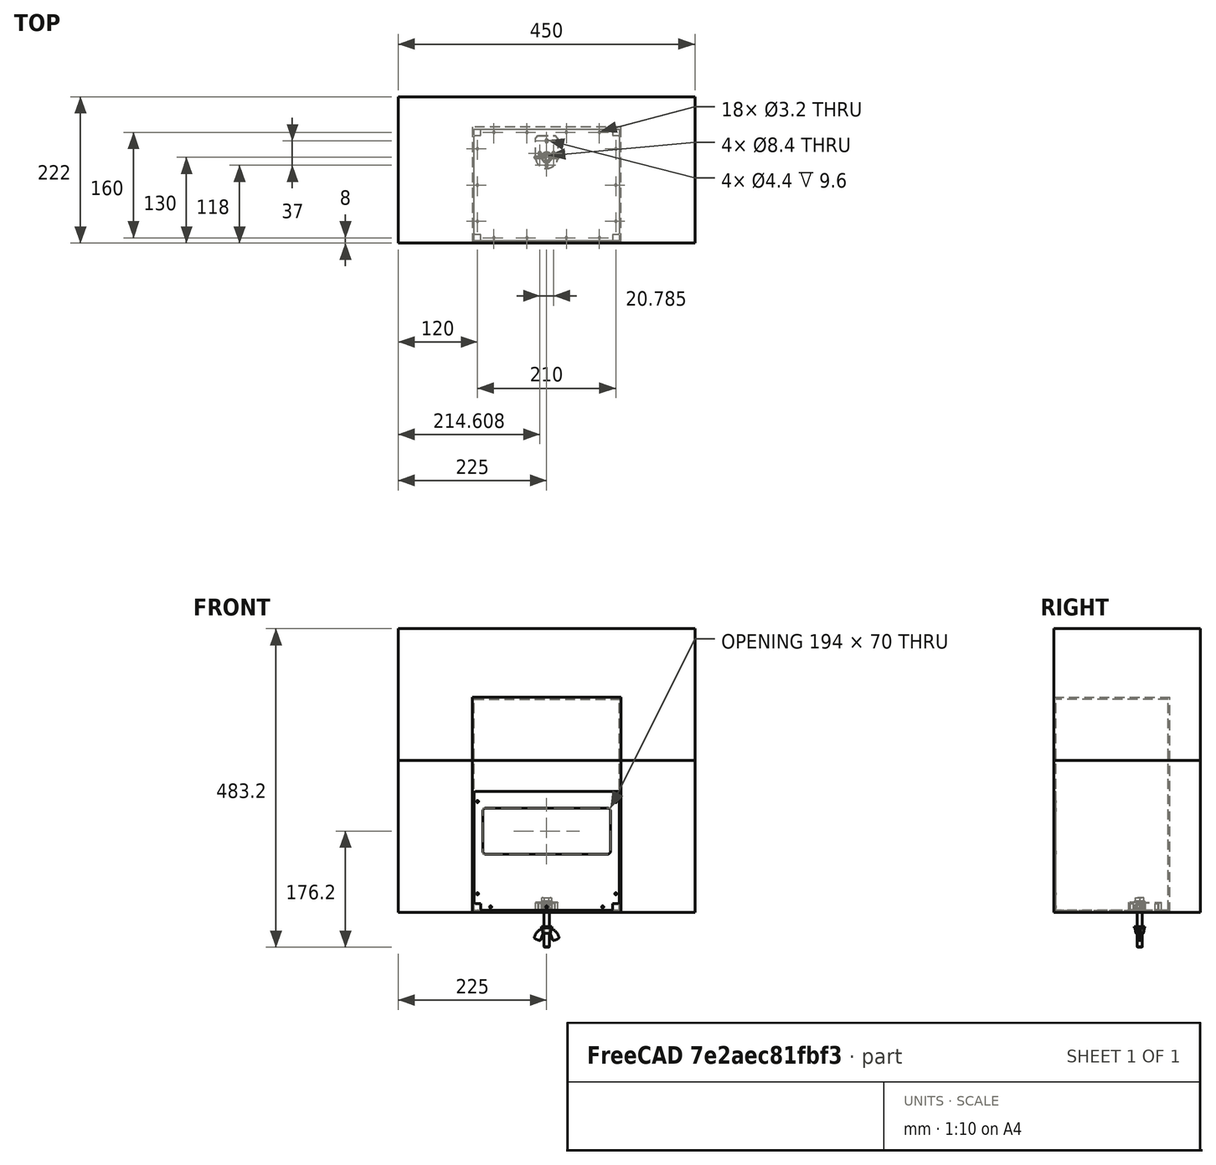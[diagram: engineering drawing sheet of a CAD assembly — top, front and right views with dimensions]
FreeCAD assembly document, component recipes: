
FREECAD ASSEMBLY — COMPONENT RECIPES ("basket_2023")

This assembly document has 8 components, labeled P0..P7 below (a component is one placed body or linked part). 6 of them carry a construction recipe — the FreeCAD feature program that regenerates the part from scratch, quoted from this document or its linked companion documents; the rest are supplied as boundary geometry only. No exploded tour is included for this assembly.
COMPONENT P0 — recipe-attached ("VolumeBasket", modeled in this document).
Construction recipe (the document's own serialized feature program — sketch geometry with constraints, then the solid features built on it; lengths are millimeters unless a unit is written):

FEATURE [Sketcher::SketchObject] Sketch
  ArcFitTolerance = 1e-06
  AttachmentSupport = -> [XY_Plane]
  ExternalBSplineMaxDegree = 5
  ExternalBSplineTolerance = 0.0001
  FullyConstrained = true
  InternalTolerance = 1e-06
  InvalidShape = false
  MakeInternals = true
  MapMode = 5
  Support = -> [XY_Plane]
  TreeRank = 12
  ValidateShape = true
  sketch-geometry (4):
    g0: LineSegment StartX=-113 StartY=3.262e-13 StartZ=0 EndX=113 EndY=1.84043e-10 EndZ=0
    g1: LineSegment StartX=113 StartY=1.84043e-10 StartZ=0 EndX=113 EndY=176 EndZ=0
    g2: LineSegment StartX=113 StartY=176 StartZ=0 EndX=-113 EndY=176 EndZ=0
    g3: LineSegment StartX=-113 StartY=176 StartZ=0 EndX=-113 EndY=3.126e-13 EndZ=0
  constraints (11):
    c: Coincident(g0,g1)
    c: Coincident(g1,g2)
    c: Coincident(g2,g3)
    c: Coincident(g3,g0)
    c: Horizontal(g2)
    c: Vertical(g1)
    c: Vertical(g3)
    c: PointOnObject(g0,g-1)
    c: Symmetric(g0,g0,g-2)
    c: DistanceX(g0,g0) = 226
    c: DistanceY(g1,g1) = 176
FEATURE [PartDesign::Pad] Pad
  AddSubType = 0
  AlongSketchNormal = false
  AutoTaperInnerAngle = true
  CheckUpToFaceLimits = true
  ClaimChildren = false
  Direction = (0,0,1)
  Fit = 0
  FitJoin = 0
  InnerFit = 0
  InnerFitJoin = 0
  InvalidShape = false
  Length = 326
  Length2 = 100
  Linearize = true
  NewSolid = false
  Profile = -> Sketch
  Refine = true
  Suppress = false
  TaperInnerAngle = 0
  TaperInnerAngleRev = 0
  TreeRank = 13
  Type = 0
  ValidateShape = true
  _ProfileBasedVersion = 1
FEATURE [PartDesign::Body] Body  label="VolumeBasket"
  AutoGroupSolids = false
  ClaimAllChildren = false
  ExportMode = 0
  Group = -> [Sketch,Pad]
  InvalidShape = false
  Origin = -> Origin
  SingleSolid = true
  Tip = -> Pad
  TreeRank = 11
  ValidateShape = true
  _ExportChildren = -> [Pad]
  _GroupVersion = 1
COMPONENT P1 — recipe-attached ("VolumeMakerBeam", modeled in this document).
Construction recipe (the document's own serialized feature program — sketch geometry with constraints, then the solid features built on it; lengths are millimeters unless a unit is written):

FEATURE [Sketcher::SketchObject] Sketch002
  ArcFitTolerance = 1e-06
  AttachmentOffset = pos=(0,0,3) rot=(0,0,1;0rad)
  AttachmentSupport = -> [XY_Plane002]
  ExternalBSplineMaxDegree = 5
  ExternalBSplineTolerance = 0.0001
  FullyConstrained = true
  InternalTolerance = 1e-06
  InvalidShape = false
  MakeInternals = true
  MapMode = 5
  Placement = pos=(0,0,3) rot=(0,0,1;0rad)
  Support = -> [XY_Plane002]
  TreeRank = 42
  ValidateShape = true
  sketch-geometry (4):
    g0: LineSegment StartX=-110 StartY=173 StartZ=0 EndX=110 EndY=173 EndZ=0
    g1: LineSegment StartX=110 StartY=173 StartZ=0 EndX=110 EndY=3 EndZ=0
    g2: LineSegment StartX=110 StartY=3 StartZ=0 EndX=-110 EndY=3 EndZ=0
    g3: LineSegment StartX=-110 StartY=3 StartZ=0 EndX=-110 EndY=173 EndZ=0
  constraints (11):
    c: Coincident(g0,g1)
    c: Coincident(g1,g2)
    c: Coincident(g2,g3)
    c: Coincident(g3,g0)
    c: Horizontal(g0)
    c: Vertical(g1)
    c: Vertical(g3)
    c: Symmetric(g1,g2,g-2)
    c: DistanceY(g-1,g1) = 3
    c: DistanceX(g2,g2) = 220
    c: DistanceY(g1,g1) = 170
FEATURE [PartDesign::Pad] Pad002
  AddSubType = 0
  AlongSketchNormal = false
  AutoTaperInnerAngle = true
  CheckUpToFaceLimits = true
  ClaimChildren = false
  Direction = (0,0,1)
  Fit = 0
  FitJoin = 0
  InnerFit = 0
  InnerFitJoin = 0
  InvalidShape = false
  Length = 320
  Length2 = 100
  Linearize = true
  NewSolid = false
  Profile = -> Sketch002
  Refine = true
  Suppress = false
  TaperInnerAngle = 0
  TaperInnerAngleRev = 0
  TreeRank = 43
  Type = 0
  ValidateShape = true
  _ProfileBasedVersion = 1
FEATURE [PartDesign::Body] Body002  label="VolumeMakerBeam"
  AutoGroupSolids = false
  ClaimAllChildren = false
  ExportMode = 0
  Group = -> [Sketch002,Pad002]
  InvalidShape = false
  Origin = -> Origin002
  SingleSolid = true
  Tip = -> Pad002
  TreeRank = 41
  ValidateShape = true
  _ExportChildren = -> [Pad002]
  _GroupVersion = 1
COMPONENT P2 — recipe-attached ("Volume300mm", modeled in this document).
Construction recipe (the document's own serialized feature program — sketch geometry with constraints, then the solid features built on it; lengths are millimeters unless a unit is written):

FEATURE [Sketcher::SketchObject] Sketch011
  ArcFitTolerance = 1e-06
  AttachmentSupport = -> [XZ_Plane006]
  ExternalBSplineMaxDegree = 5
  ExternalBSplineTolerance = 0.0001
  FullyConstrained = true
  InternalTolerance = 1e-06
  InvalidShape = false
  MakeInternals = true
  MapMode = 5
  Placement = pos=(0,0,0) rot=(1,0,0;1.5708rad)
  Support = -> [XZ_Plane006]
  TreeRank = 153
  ValidateShape = true
  sketch-geometry (4):
    g0: LineSegment StartX=-225 StartY=430 StartZ=0 EndX=225 EndY=430 EndZ=0
    g1: LineSegment StartX=225 StartY=430 StartZ=0 EndX=225 EndY=230 EndZ=0
    g2: LineSegment StartX=225 StartY=230 StartZ=0 EndX=-225 EndY=230 EndZ=0
    g3: LineSegment StartX=-225 StartY=230 StartZ=0 EndX=-225 EndY=430 EndZ=0
  constraints (11):
    c: Coincident(g0,g1)
    c: Coincident(g1,g2)
    c: Coincident(g2,g3)
    c: Coincident(g3,g0)
    c: Horizontal(g0)
    c: Vertical(g1)
    c: Vertical(g3)
    c: DistanceY(g0) = 430
    c: DistanceX(g0,g0) = 450
    c: Symmetric(g1,g2,g-2)
    c: DistanceY(g1) = 230
FEATURE [PartDesign::Pad] Pad007
  AddSubType = 0
  AlongSketchNormal = false
  AutoTaperInnerAngle = true
  CheckUpToFaceLimits = true
  ClaimChildren = false
  Direction = (0,-1,2e-16)
  Fit = 0
  FitJoin = 0
  InnerFit = 0
  InnerFitJoin = 0
  InvalidShape = false
  Length = 222
  Length2 = 100
  Linearize = true
  NewSolid = false
  Profile = -> Sketch011
  Refine = true
  Reversed = true
  Suppress = false
  TaperInnerAngle = 0
  TaperInnerAngleRev = 0
  TreeRank = 154
  Type = 0
  ValidateShape = true
  _ProfileBasedVersion = 1
FEATURE [PartDesign::Body] Body006  label="Volume300mm"
  AutoGroupSolids = false
  ClaimAllChildren = false
  ExportMode = 0
  Group = -> [Sketch011,Pad007]
  InvalidShape = false
  Origin = -> Origin009
  SingleSolid = true
  Tip = -> Pad007
  TreeRank = 152
  ValidateShape = true
  _ExportChildren = -> [Pad007]
  _GroupVersion = 1
COMPONENT P3 — recipe-attached ("Link(MB_300)", modeled in this document).
Construction recipe (the document's own serialized feature program — sketch geometry with constraints, then the solid features built on it; lengths are millimeters unless a unit is written):

FEATURE [Sketcher::SketchObject] Sketch006
  ArcFitTolerance = 1e-06
  AttachmentSupport = -> [XY_Plane004]
  ExternalBSplineMaxDegree = 5
  ExternalBSplineTolerance = 0.0001
  ExternalGeometry = -> [Pocket001]
  FullyConstrained = true
  InternalTolerance = 1e-06
  InvalidShape = false
  MakeInternals = true
  MapMode = 5
  Support = -> [XY_Plane004]
  TreeRank = 93
  ValidateShape = true
  sketch-geometry (5):
    g0: ArcOfCircle CenterX=-1.78743e-11 CenterY=130 CenterZ=0 NormalX=0 NormalY=0 NormalZ=1 AngleXU=0 Radius=17 StartAngle=3.14159 EndAngle=6.28319
    g1: LineSegment StartX=-17 StartY=130 StartZ=0 EndX=-17 EndY=163 EndZ=0
    g2: LineSegment StartX=-17 StartY=163 StartZ=0 EndX=17 EndY=163 EndZ=0
    g3: LineSegment StartX=17 StartY=163 StartZ=0 EndX=17 EndY=130 EndZ=0
    g4: Circle CenterX=-1.78743e-11 CenterY=130 CenterZ=0 NormalX=0 NormalY=0 NormalZ=1 AngleXU=0 Radius=4.2
  constraints (12):
    c: Coincident(g0,g-3)
    c: Vertical(g1)
    c: Coincident(g2,g1)
    c: Horizontal(g2)
    c: Coincident(g3,g2)
    c: Vertical(g3)
    c: DistanceY(g2,g-4) = 10
    c: Tangent(g3,g0) = 1.5708
    c: Tangent(g1,g0) = 1.5708
    c: Diameter(g0) = 34
    c: Coincident(g4,g0)
    c: Diameter(g4) = 8.4
FEATURE [PartDesign::Pad] Pad004
  AddSubType = 0
  AlongSketchNormal = false
  AutoTaperInnerAngle = true
  CheckUpToFaceLimits = true
  ClaimChildren = false
  Direction = (0,0,1)
  Fit = 0
  FitJoin = 0
  InnerFit = 0
  InnerFitJoin = 0
  InvalidShape = false
  Length = 12
  Length2 = 100
  Linearize = true
  NewSolid = false
  Profile = -> Sketch006
  Refine = true
  Suppress = false
  TaperInnerAngle = 0
  TaperInnerAngleRev = 0
  TreeRank = 104
  Type = 0
  ValidateShape = true
  _ProfileBasedVersion = 1
FEATURE [Sketcher::SketchObject] Sketch007
  ArcFitTolerance = 1e-06
  AttachmentSupport = -> [XY_Plane004]
  ExternalBSplineMaxDegree = 5
  ExternalBSplineTolerance = 0.0001
  ExternalGeometry = -> [Pad004]
  FullyConstrained = true
  InternalTolerance = 1e-06
  InvalidShape = false
  MakeInternals = true
  MapMode = 5
  Support = -> [XY_Plane004]
  TreeRank = 105
  ValidateShape = true
  sketch-geometry (7):
    g0: LineSegment StartX=7.79423 StartY=130 StartZ=0 EndX=3.89711 EndY=136.75 EndZ=0
    g1: LineSegment StartX=3.89711 StartY=136.75 StartZ=0 EndX=-3.89711 EndY=136.75 EndZ=0
    g2: LineSegment StartX=-3.89711 StartY=136.75 StartZ=0 EndX=-7.79423 EndY=130 EndZ=0
    g3: LineSegment StartX=-7.79423 StartY=130 StartZ=0 EndX=-3.89711 EndY=123.25 EndZ=0
    g4: LineSegment StartX=-3.89711 StartY=123.25 StartZ=0 EndX=3.89711 EndY=123.25 EndZ=0
    g5: LineSegment StartX=3.89711 StartY=123.25 StartZ=0 EndX=7.79423 EndY=130 EndZ=0
    g6: Circle [constr] CenterX=2.73045e-11 CenterY=130 CenterZ=0 NormalX=0 NormalY=0 NormalZ=1 AngleXU=0 Radius=7.79423
  constraints (16):
    c: Coincident(g0,g1)
    c: Coincident(g1,g2)
    c: Coincident(g2,g3)
    c: Coincident(g3,g4)
    c: Coincident(g4,g5)
    c: Coincident(g5,g0)
    c: Equal(g0, g1-g5) x5
    c: PointOnObject(g0,g6)
    c: PointOnObject(g1,g6)
    c: PointOnObject(g2,g6)
    c: PointOnObject(g3,g6)
    c: PointOnObject(g4,g6)
    c: PointOnObject(g5,g6)
    c: Coincident(g6,g-3)
    c: Horizontal(g1)
    c: DistanceY(g4,g0) = 13.5
FEATURE [PartDesign::Pad] Pad005
  AddSubType = 1
  AlongSketchNormal = false
  AutoTaperInnerAngle = true
  BaseFeature = -> Pad004
  CheckUpToFaceLimits = true
  ClaimChildren = false
  Direction = (0,0,1)
  Fit = 0
  FitJoin = 0
  InnerFit = 0
  InnerFitJoin = 0
  InvalidShape = false
  Length = 8.5
  Length2 = 100
  Linearize = true
  NewSolid = false
  Profile = -> Sketch007
  Refine = true
  Suppress = false
  TaperInnerAngle = 0
  TaperInnerAngleRev = 0
  TreeRank = 106
  Type = 0
  ValidateShape = true
  _ProfileBasedVersion = 1
FEATURE [Sketcher::SketchObject] Sketch008
  ArcFitTolerance = 1e-06
  AttachmentSupport = -> [XY_Plane004]
  ExternalBSplineMaxDegree = 5
  ExternalBSplineTolerance = 0.0001
  ExternalGeometry = -> [Pad004]
  FullyConstrained = true
  InternalTolerance = 1e-06
  InvalidShape = false
  MakeInternals = true
  MapMode = 5
  Support = -> [XY_Plane004]
  TreeRank = 107
  ValidateShape = true
  sketch-geometry (7):
    g0: Circle CenterX=1.1e-15 CenterY=118 CenterZ=0 NormalX=0 NormalY=0 NormalZ=1 AngleXU=0 Radius=2.2
    g1: Circle CenterX=-10.3923 CenterY=136 CenterZ=0 NormalX=0 NormalY=0 NormalZ=1 AngleXU=0 Radius=2.2
    g2: Circle CenterX=10.3923 CenterY=136 CenterZ=0 NormalX=0 NormalY=0 NormalZ=1 AngleXU=0 Radius=2.2
    g3: Circle [constr] CenterX=-4.19335e-11 CenterY=130 CenterZ=0 NormalX=0 NormalY=0 NormalZ=1 AngleXU=0 Radius=12
    g4: Circle CenterX=0 CenterY=155 CenterZ=0 NormalX=0 NormalY=0 NormalZ=1 AngleXU=0 Radius=2.2
    g5: LineSegment [constr] StartX=-1.80398e-11 StartY=130 StartZ=0 EndX=-10.3923 EndY=136 EndZ=0
    g6: LineSegment [constr] StartX=-1.79352e-11 StartY=130 StartZ=0 EndX=10.3923 EndY=136 EndZ=0
  constraints (18):
    c: PointOnObject(g0,g-2)
    c: Coincident(g3,g-3)
    c: PointOnObject(g2,g3)
    c: PointOnObject(g0,g3)
    c: PointOnObject(g1,g3)
    c: Equal(g1,g2)
    c: Equal(g1,g0)
    c: Diameter(g1) = 4.4
    c: PointOnObject(g4,g-2)
    c: Equal(g4,g2)
    c: Coincident(g5,g-3)
    c: Coincident(g5,g1)
    c: Coincident(g6,g-3)
    c: Coincident(g6,g2)
    c: Angle(g-2,g6) = 2.0944
    c: Angle(g5,g-2) = 2.0944
    c: DistanceY(g0,g-3) = 12
    c: DistanceY(g-3,g4) = 25
FEATURE [PartDesign::Pocket] Pocket002
  AddSubType = 1
  AutoTaperInnerAngle = true
  BaseFeature = -> Pad005
  CheckUpToFaceLimits = true
  ClaimChildren = false
  Fit = 0
  FitJoin = 0
  InnerFit = 0
  InnerFitJoin = 0
  InvalidShape = false
  Length = 10
  Length2 = 100
  Linearize = true
  NewSolid = false
  Profile = -> Sketch008
  Refine = true
  Reversed = true
  Suppress = false
  TaperInnerAngle = 0
  TaperInnerAngleRev = 0
  TreeRank = 108
  Type = 0
  ValidateShape = true
  _ProfileBasedVersion = 1
  _Version = 1
FEATURE [PartDesign::Chamfer] Chamfer001
  AddSubType = 0
  Angle = 45
  Base = -> Pocket002 [Edge8,Edge5]
  BaseFeature = -> Pocket002
  ChamferType = 0
  FlipDirection = false
  InvalidShape = false
  NewSolid = false
  Refine = true
  Size = 4
  Size2 = 1
  SupportTransform = false
  Suppress = false
  TreeRank = 119
  ValidateShape = true
FEATURE [PartDesign::Chamfer] Chamfer002
  AddSubType = 0
  Angle = 45
  Base = -> Chamfer001 [Face2,Edge50,Face5]
  BaseFeature = -> Chamfer001
  ChamferType = 0
  FlipDirection = false
  InvalidShape = false
  NewSolid = false
  Refine = true
  Size = 0.4
  Size2 = 1
  SupportTransform = false
  Suppress = false
  TreeRank = 120
  ValidateShape = true
FEATURE [PartDesign::Body] Body004  label="BlocVisPapillon"
  AutoGroupSolids = false
  ClaimAllChildren = false
  ExportMode = 0
  Group = -> [Sketch006,Pad004,Sketch007,Pad005,Sketch008,Pocket002,Chamfer001,Chamfer002]
  InvalidShape = false
  Origin = -> Origin005
  Placement = pos=(0,0,3) rot=(0,0,1;0rad)
  SingleSolid = true
  Tip = -> Chamfer002
  TreeRank = 136
  ValidateShape = true
  _ExportChildren = -> [Pad004,Pad005,Pocket002,Chamfer001,Chamfer002]
  _GroupVersion = 1
COMPONENT P4 — geometry summary ("Link001(MB_200)"; no construction recipe available for this part):
  bounding box: 200.0 x 10.0 x 10.0 mm
  tessellated surface: 288 triangles
  volume: 9738 mm^3 (49% of its bounding box)
  symmetry: 2-fold rotationally symmetric about the x axis; 4-fold rotationally symmetric about the y axis; 2-fold rotationally symmetric about the z axis; mirror-symmetric across its x mid-plane, y mid-plane, z mid-plane
COMPONENT P5 — geometry summary ("Link002(MB_150)"; no construction recipe available for this part):
  bounding box: 150.0 x 10.0 x 10.0 mm
  tessellated surface: 288 triangles
  volume: 7304 mm^3 (49% of its bounding box)
  symmetry: 2-fold rotationally symmetric about the x axis; 4-fold rotationally symmetric about the y axis; 2-fold rotationally symmetric about the z axis; mirror-symmetric across its y mid-plane, z mid-plane
COMPONENT P6 — recipe-attached ("Link003(Corner)", modeled in this document).
Construction recipe (the document's own serialized feature program — sketch geometry with constraints, then the solid features built on it; lengths are millimeters unless a unit is written):

FEATURE [Sketcher::SketchObject] Sketch001
  ArcFitTolerance = 1e-06
  AttachmentSupport = -> [XY_Plane001]
  ExternalBSplineMaxDegree = 5
  ExternalBSplineTolerance = 0.0001
  FullyConstrained = true
  InternalTolerance = 1e-06
  InvalidShape = false
  MakeInternals = true
  MapMode = 5
  Support = -> [XY_Plane001]
  TreeRank = 30
  ValidateShape = true
  sketch-geometry (4):
    g0: LineSegment StartX=-225 StartY=-3.837e-13 StartZ=0 EndX=225 EndY=-3.837e-13 EndZ=0
    g1: LineSegment StartX=225 StartY=-3.837e-13 StartZ=0 EndX=225 EndY=222 EndZ=0
    g2: LineSegment StartX=225 StartY=222 StartZ=0 EndX=-225 EndY=222 EndZ=0
    g3: LineSegment StartX=-225 StartY=222 StartZ=0 EndX=-225 EndY=-3.695e-13 EndZ=0
  constraints (11):
    c: Coincident(g0,g1)
    c: Coincident(g1,g2)
    c: Coincident(g2,g3)
    c: Coincident(g3,g0)
    c: Horizontal(g0)
    c: Horizontal(g2)
    c: Vertical(g1)
    c: Vertical(g3)
    c: Symmetric(g0,g0,g-1)
    c: DistanceY(g1,g1) = 222
    c: DistanceX(g0,g0) = 450
FEATURE [PartDesign::Pad] Pad001
  AddSubType = 0
  AlongSketchNormal = false
  AutoTaperInnerAngle = true
  CheckUpToFaceLimits = true
  ClaimChildren = false
  Direction = (0,0,1)
  Fit = 0
  FitJoin = 0
  InnerFit = 0
  InnerFitJoin = 0
  InvalidShape = false
  Length = 430
  Length2 = 100
  Linearize = true
  NewSolid = false
  Profile = -> Sketch001
  Refine = true
  Suppress = false
  TaperInnerAngle = 0
  TaperInnerAngleRev = 0
  TreeRank = 31
  Type = 0
  ValidateShape = true
  _ProfileBasedVersion = 1
FEATURE [PartDesign::Body] Body001  label="VolumeMax"
  AutoGroupSolids = false
  ClaimAllChildren = false
  ExportMode = 0
  Group = -> [Sketch001,Pad001]
  InvalidShape = false
  Origin = -> Origin001
  SingleSolid = true
  Tip = -> Pad001
  TreeRank = 29
  ValidateShape = true
  _ExportChildren = -> [Pad001]
  _GroupVersion = 1
COMPONENT P7 — recipe-attached ("Basket_2023", modeled in this document).
Construction recipe (the document's own serialized feature program — sketch geometry with constraints, then the solid features built on it; lengths are millimeters unless a unit is written):

FEATURE [Sketcher::SketchObject] Sketch010
  ArcFitTolerance = 1e-06
  AttachmentSupport = -> [XZ_Plane005]
  ExternalBSplineMaxDegree = 5
  ExternalBSplineTolerance = 0.0001
  FullyConstrained = true
  InternalTolerance = 1e-06
  InvalidShape = false
  MakeInternals = true
  MapMode = 5
  Placement = pos=(0,0,0) rot=(1,0,0;1.5708rad)
  Support = -> [XZ_Plane005]
  TreeRank = 131
  ValidateShape = true
  sketch-geometry (28):
    g0: LineSegment StartX=-100 StartY=3 StartZ=0 EndX=-100 EndY=13 EndZ=0
    g1: LineSegment StartX=-100 StartY=13 StartZ=0 EndX=-110 EndY=13 EndZ=0
    g2: LineSegment StartX=-110 StartY=13 StartZ=0 EndX=-110 EndY=183 EndZ=0
    g3: LineSegment StartX=-110 StartY=183 StartZ=0 EndX=110 EndY=183 EndZ=0
    g4: LineSegment StartX=110 StartY=183 StartZ=0 EndX=110 EndY=13 EndZ=0
    g5: LineSegment StartX=110 StartY=13 StartZ=0 EndX=100 EndY=13 EndZ=0
    g6: LineSegment StartX=100 StartY=13 StartZ=0 EndX=100 EndY=3 EndZ=0
    g7: LineSegment StartX=100 StartY=3 StartZ=0 EndX=-100 EndY=3 EndZ=0
    g8: ArcOfCircle CenterX=-92 CenterY=153 CenterZ=0 NormalX=0 NormalY=0 NormalZ=1 AngleXU=0 Radius=5 StartAngle=1.5708 EndAngle=3.14159
    g9: LineSegment StartX=-92 StartY=158 StartZ=0 EndX=92 EndY=158 EndZ=0
    g10: ArcOfCircle CenterX=92 CenterY=153 CenterZ=0 NormalX=0 NormalY=0 NormalZ=1 AngleXU=0 Radius=5 StartAngle=-9e-16 EndAngle=1.5708
    g11: LineSegment StartX=97 StartY=153 StartZ=0 EndX=97 EndY=93 EndZ=0
    g12: ArcOfCircle CenterX=92 CenterY=93 CenterZ=0 NormalX=0 NormalY=0 NormalZ=1 AngleXU=0 Radius=5 StartAngle=4.71239 EndAngle=6.28319
    g13: LineSegment StartX=92 StartY=88 StartZ=0 EndX=-92 EndY=88 EndZ=0
    g14: ArcOfCircle CenterX=-92 CenterY=93 CenterZ=0 NormalX=0 NormalY=0 NormalZ=1 AngleXU=0 Radius=5 StartAngle=3.14159 EndAngle=4.71239
    g15: LineSegment StartX=-97 StartY=93 StartZ=0 EndX=-97 EndY=153 EndZ=0
    g16: GeomPoint [constr] X=-97 Y=158 Z=0
    g17: GeomPoint [constr] X=97 Y=88 Z=0
    g18: LineSegment [constr] StartX=-100 StartY=8 StartZ=0 EndX=100 EndY=8 EndZ=0
    g19: LineSegment [constr] StartX=105 StartY=13 StartZ=0 EndX=105 EndY=183 EndZ=0
    g20: LineSegment [constr] StartX=-105 StartY=13 StartZ=0 EndX=-105 EndY=183 EndZ=0
    g21: Circle CenterX=-105 CenterY=168 CenterZ=0 NormalX=0 NormalY=0 NormalZ=1 AngleXU=0 Radius=1.6
    g22: Circle CenterX=-105 CenterY=28 CenterZ=0 NormalX=0 NormalY=0 NormalZ=1 AngleXU=0 Radius=1.6
    g23: Circle CenterX=-85 CenterY=8 CenterZ=0 NormalX=0 NormalY=0 NormalZ=1 AngleXU=0 Radius=1.6
    g24: Circle CenterX=85 CenterY=8 CenterZ=0 NormalX=0 NormalY=0 NormalZ=1 AngleXU=0 Radius=1.6
    g25: Circle CenterX=105 CenterY=28 CenterZ=0 NormalX=0 NormalY=0 NormalZ=1 AngleXU=0 Radius=1.6
    g26: Circle CenterX=105 CenterY=168 CenterZ=0 NormalX=0 NormalY=0 NormalZ=1 AngleXU=0 Radius=1.6
    g27: Circle CenterX=0 CenterY=8 CenterZ=0 NormalX=0 NormalY=0 NormalZ=1 AngleXU=0 Radius=1.6
  constraints (73):
    c: Vertical(g0)
    c: Coincident(g0,g1)
    c: Horizontal(g1)
    c: Coincident(g1,g2)
    c: Vertical(g2)
    c: Coincident(g2,g3)
    c: Horizontal(g3)
    c: Coincident(g3,g4)
    c: Vertical(g4)
    c: Coincident(g4,g5)
    c: Horizontal(g5)
    c: Coincident(g5,g6)
    c: Coincident(g6,g7)
    c: Coincident(g7,g0)
    c: Vertical(g6)
    c: Equal(g6,g5)
    c: Equal(g5,g0)
    c: Equal(g0,g1)
    c: DistanceX(g5,g5) = 10
    c: DistanceY(g6) = 3
    c: Symmetric(g6,g0,g-2)
    c: DistanceX(g1,g4) = 220
    c: Tangent(g8,g9) = 1.5708
    c: Tangent(g9,g10) = 1.5708
    c: Tangent(g10,g11) = 1.5708
    c: Tangent(g11,g12) = 1.5708
    c: Tangent(g12,g13) = 1.5708
    c: Tangent(g13,g14) = 1.5708
    c: Tangent(g14,g15) = 1.5708
    c: Tangent(g15,g8) = 1.5708
    c: Horizontal(g9)
    c: Horizontal(g13)
    c: Vertical(g11)
    c: Vertical(g15)
    c: Equal(g8,g10)
    c: Equal(g10,g12)
    c: PointOnObject(g16,g9)
    c: PointOnObject(g16,g15)
    c: PointOnObject(g17,g11)
    c: PointOnObject(g17,g13)
    c: DistanceY(g-1,g12) = 88
    c: Symmetric(g14,g12,g-2)
    c: DistanceY(g6,g3) = 180
    c: DistanceX(g0,g14) = 3
    c: DistanceY(g12,g9) = 70
    c: Radius(g8) = 5
    c: PointOnObject(g18,g0)
    c: Horizontal(g18)
    c: Symmetric(g6,g5,g18)
    c: PointOnObject(g19,g3)
    c: Vertical(g19)
    c: Symmetric(g5,g4,g19)
    c: PointOnObject(g20,g3)
    c: Vertical(g20)
    c: Symmetric(g1,g0,g20)
    c: PointOnObject(g21,g20)
    c: PointOnObject(g22,g20)
    c: PointOnObject(g23,g18)
    c: Equal(g26,g25)
    c: Equal(g26,g24)
    c: Equal(g26,g23)
    c: Equal(g26,g22)
    c: Equal(g26,g21)
    c: Diameter(g26) = 3.2
    c: Symmetric(g21,g26,g-2)
    c: Symmetric(g25,g22,g-2)
    c: Symmetric(g23,g24,g-2)
    c: DistanceY(g21,g20) = 15
    c: DistanceY(g20,g22) = 15
    c: DistanceX(g18,g23) = 15
    c: Equal(g27,g24)
    c: PointOnObject(g27,g18)
    c: PointOnObject(g27,g-2)
FEATURE [PartDesign::Pad] Pad006
  AddSubType = 0
  AlongSketchNormal = false
  AutoTaperInnerAngle = true
  CheckUpToFaceLimits = true
  ClaimChildren = false
  Direction = (0,-1,-2e-16)
  Fit = 0
  FitJoin = 0
  InnerFit = 0
  InnerFitJoin = 0
  InvalidShape = false
  Length = 3
  Length2 = 100
  Linearize = true
  NewSolid = false
  Profile = -> Sketch010
  Refine = true
  Reversed = true
  Suppress = false
  TaperInnerAngle = 0
  TaperInnerAngleRev = 0
  TreeRank = 132
  Type = 0
  ValidateShape = true
  _ProfileBasedVersion = 1
FEATURE [PartDesign::Chamfer] Chamfer003
  AddSubType = 0
  Angle = 45
  Base = -> Pad006 [Edge14,Edge20,Edge1,Edge5,Edge8,Edge11]
  BaseFeature = -> Pad006
  ChamferType = 0
  FlipDirection = false
  InvalidShape = false
  NewSolid = false
  Refine = true
  Size = 1.5
  Size2 = 1
  SupportTransform = false
  Suppress = false
  TreeRank = 133
  ValidateShape = true
FEATURE [PartDesign::Body] Body005  label="CarterAvantOuverture"
  AutoGroupSolids = false
  ClaimAllChildren = false
  ExportMode = 0
  Group = -> [Sketch010,Pad006,Chamfer003]
  InvalidShape = false
  Origin = -> Origin006
  SingleSolid = true
  Tip = -> Chamfer003
  TreeRank = 130
  ValidateShape = true
  _ExportChildren = -> [Pad006,Chamfer003]
  _GroupVersion = 1
PROVENANCE & LICENSES
A FreeCAD (.FCStd) document from a public repository crawl; recipes are the document's own serialized feature recipes (and, for linked parts, companion documents' recipes).
License: mit.
